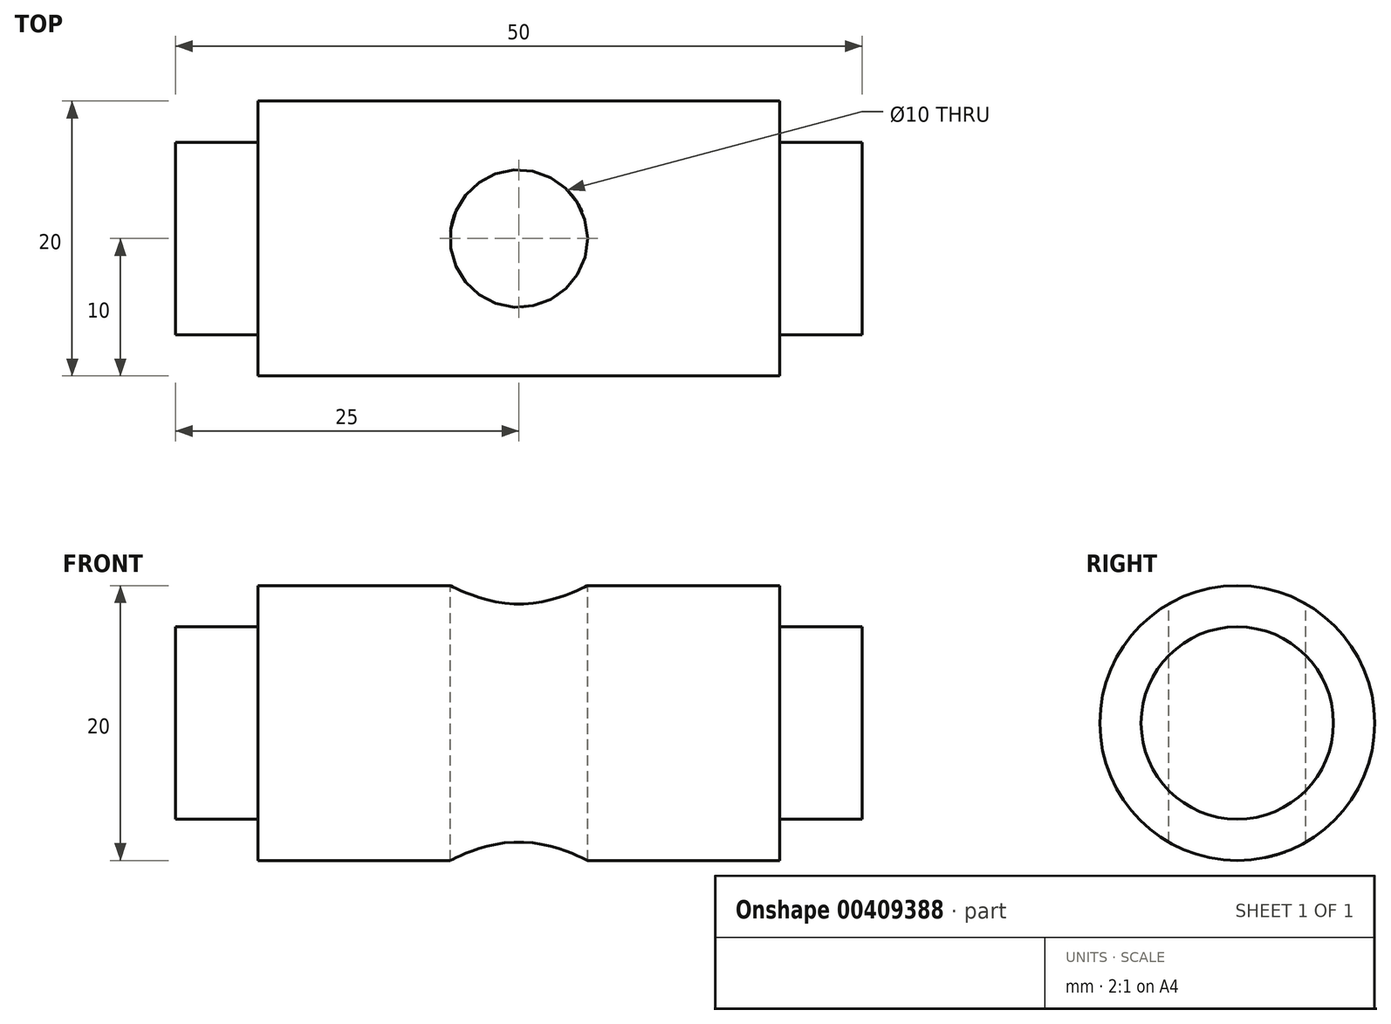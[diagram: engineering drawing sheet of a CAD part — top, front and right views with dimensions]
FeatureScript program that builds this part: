
annotation { "Feature Type Name" : "Feature", "Feature Type Description" : "" }
export const myFeature = defineFeature(function(context is Context, id is Id, definition is map)
    precondition{}
    {
        {
            var Q0;
            Q0=qCreatedBy(makeId("Front.planeOp"),FACE);
            var sketch = newSketch(context, id + "F0", { "sketchPlane" : qUnion([Q0])});
            skLineSegment(sketch, "E0", {"start": v(0, 0) * mm, "end": v(0, 7) * mm});
            skLineSegment(sketch, "E1", {"start": v(0, 7) * mm, "end": v(6, 7) * mm});
            skLineSegment(sketch, "E2", {"start": v(6, 7) * mm, "end": v(6, 10) * mm});
            skLineSegment(sketch, "E3", {"start": v(6, 10) * mm, "end": v(44, 10) * mm});
            skLineSegment(sketch, "E4", {"start": v(44, 10) * mm, "end": v(44, 7) * mm});
            skLineSegment(sketch, "E5", {"start": v(44, 7) * mm, "end": v(50, 7) * mm});
            skLineSegment(sketch, "E6", {"start": v(50, 7) * mm, "end": v(50, 0) * mm});
            skLineSegment(sketch, "E7", {"start": v(50, 0) * mm, "end": v(0, 0) * mm});
            skSolve(sketch);
        }
        {
            var Q0;
            Q0=makeQuery(id+"F0.imprint","IMPRINT",FACE,{"disambiguationData":[TD([[makeQuery(id+"F0.imprint","IMPRINT",EDGE,{"derivedFrom":sQuery(id+"F0.wireOp",EDGE,"E0")}),-1.0]])]});
            var Q1;
            Q1=sQuery(id+"F0.wireOp",EDGE,"E7");
            revolve(context, id + "F1", {"entities" : qUnion([Q0]), "axis" : qUnion([Q1]), "revolveType" : RevolveType.FULL});
        }
        {
            var Q0;
            Q0=qCreatedBy(makeId("Top.planeOp"),FACE);
            cPlane(context, id + "F2", {"entities" : qUnion([Q0]), "cplaneType" : CPlaneType.OFFSET, "offset" : 10 * mm, "width" : 150 * mm, "height" : 150 * mm});
        }
        {
            var Q0;
            Q0=qCreatedBy(id+"F2.planeOp",FACE);
            var sketch = newSketch(context, id + "F3", { "sketchPlane" : qUnion([Q0])});
            skCircle(sketch, "E8", {"center": v(25, 0) * mm, "radius": 5 * mm});
            skSolve(sketch);
        }
        {
            var Q0;
            Q0=makeQuery(id+"F3.imprint","IMPRINT",FACE,{"disambiguationData":[TD([[makeQuery(id+"F3.imprint","IMPRINT",EDGE,{"derivedFrom":sQuery(id+"F3.wireOp",EDGE,"E8")}),1.0]])]});
            extrude(context, id + "F4", {"entities" : qUnion([Q0]), "operationType" : NewBodyOperationType.REMOVE, "endBound" : BoundingType.THROUGH_ALL, "oppositeDirection" : true, "depth" : 25 * mm});
        }
    });
